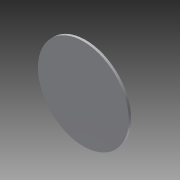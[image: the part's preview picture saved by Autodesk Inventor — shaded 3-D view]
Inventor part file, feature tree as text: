
AUTODESK INVENTOR PART (.ipt)
format: ipt  version: 2014 (Build 180170000, 170)  size: 242,688 bytes
history: native  units: mm
features: extrude x5, sketch x5, fillet x1
ambient origin geometry x8: Origin, YZ Plane, XZ Plane, XY Plane, X Axis, Y Axis, Z Axis, Center Point
bodies: Solid1 (feature_tree)
feature tree (11):
  extrude  "Extrusion1"  Depth=2.0mm TaperAngle=0.0deg
  extrude  "Extrusion2"  Depth=60.0mm TaperAngle=360.0deg
  extrude  "Extrusion3"  Depth=50.0mm
  extrude  "Extrusion4"  Depth=50.0mm
  fillet  "Fillet1"  Radius=50.0mm
  extrude  "Extrusion5"  Depth=70.0mm
  sketch  "Sketch1"  dims[d0=155.0mm d4=2.0mm d5=0.0mm]
  sketch  "Sketch2"  dims[d15=0.436332mm d16=60.0mm d18=360.0deg]
  sketch  "Sketch3"  dims[d21=50.0mm d22=50.0mm]
  sketch  "Sketch4"  dims[d23=50.0mm d24=50.0mm d25=50.0mm]
  sketch  "Sketch5"  dims[d26=50.0mm d28=70.0mm d29=70.0mm d30=70.0mm d31=70.0mm d32=70.0mm d33=70.0mm d34=5.0mm d35=2.0mm d36=0.0mm d37=12.8mm d38=6.6mm d39=0.0mm d40=4.4mm d41=12.0mm d42=0.0mm d43=5.0mm d44=79.0mm d45=75.0mm d46=1.0mm d47=0.0mm]
